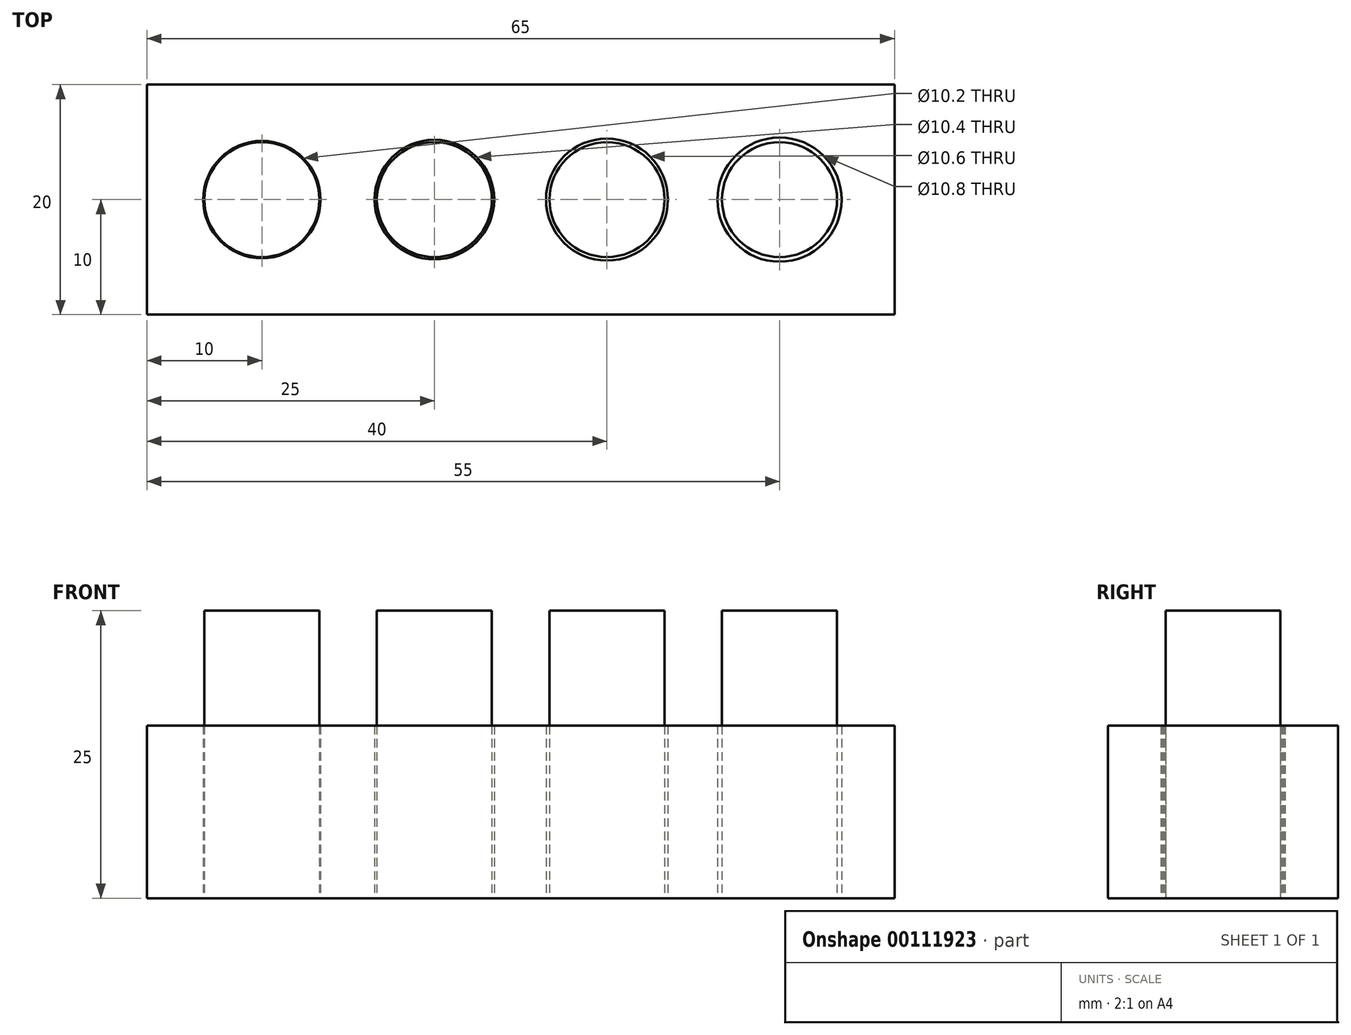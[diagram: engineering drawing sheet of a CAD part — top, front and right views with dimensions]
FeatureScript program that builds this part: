
annotation { "Feature Type Name" : "Feature", "Feature Type Description" : "" }
export const myFeature = defineFeature(function(context is Context, id is Id, definition is map)
    precondition{}
    {
        {
            var Q0;
            Q0=qCreatedBy(makeId("Top.planeOp"),FACE);
            var sketch = newSketch(context, id + "F0", { "sketchPlane" : qUnion([Q0])});
            skCircle(sketch, "E0", {"center": v(0, 0) * mm, "radius": 5 * mm});
            skCircle(sketch, "E1.1.0.0", {"center": v(15, 0) * mm, "radius": 5 * mm});
            skCircle(sketch, "E1.2.0.0", {"center": v(30, 0) * mm, "radius": 5 * mm});
            skCircle(sketch, "E1.3.0.0", {"center": v(45, 0) * mm, "radius": 5 * mm});
            skLineSegment(sketch, "E1.direction1", {"start": v(0, 0) * mm, "end": v(15, 0) * mm, "construction": true});
            skLineSegment(sketch, "E2.bottom", {"start": v(-10, 10) * mm, "end": v(55, 10) * mm});
            skLineSegment(sketch, "E2.top", {"start": v(-10, -10) * mm, "end": v(55, -10) * mm});
            skLineSegment(sketch, "E2.left", {"start": v(-10, 10) * mm, "end": v(-10, -10) * mm});
            skLineSegment(sketch, "E2.right", {"start": v(55, 10) * mm, "end": v(55, -10) * mm});
            skCircle(sketch, "E3.0", {"center": v(0, 0) * mm, "radius": 5.1 * mm});
            skCircle(sketch, "E4.0", {"center": v(15, 0) * mm, "radius": 5.2 * mm});
            skCircle(sketch, "E5.0", {"center": v(30, 0) * mm, "radius": 5.3 * mm});
            skCircle(sketch, "E6.0", {"center": v(45, 0) * mm, "radius": 5.4 * mm});
            skSolve(sketch);
        }
        {
            var Q0;
            Q0=makeQuery(id+"F0.imprint","IMPRINT",FACE,{"disambiguationData":[TD([[makeQuery(id+"F0.imprint","IMPRINT",EDGE,{"derivedFrom":sQuery(id+"F0.wireOp",EDGE,"E2.bottom")}),-1.0]])]});
            extrude(context, id + "F1", {"entities" : qUnion([Q0]), "depth" : 15 * mm});
        }
        {
            var Q0;
            Q0=makeQuery(id+"F0.imprint","IMPRINT",FACE,{"disambiguationData":[TD([[makeQuery(id+"F0.imprint","IMPRINT",EDGE,{"derivedFrom":sQuery(id+"F0.wireOp",EDGE,"E0")}),1.0]])]});
            var Q1;
            Q1=makeQuery(id+"F0.imprint","IMPRINT",FACE,{"disambiguationData":[TD([[makeQuery(id+"F0.imprint","IMPRINT",EDGE,{"derivedFrom":sQuery(id+"F0.wireOp",EDGE,"E1.1.0.0")}),1.0]])]});
            var Q2;
            Q2=makeQuery(id+"F0.imprint","IMPRINT",FACE,{"disambiguationData":[TD([[makeQuery(id+"F0.imprint","IMPRINT",EDGE,{"derivedFrom":sQuery(id+"F0.wireOp",EDGE,"E1.2.0.0")}),1.0]])]});
            var Q3;
            Q3=makeQuery(id+"F0.imprint","IMPRINT",FACE,{"disambiguationData":[TD([[makeQuery(id+"F0.imprint","IMPRINT",EDGE,{"derivedFrom":sQuery(id+"F0.wireOp",EDGE,"E1.3.0.0")}),1.0]])]});
            extrude(context, id + "F2", {"entities" : qUnion([Q0, Q1, Q2, Q3]), "depth" : 25 * mm});
        }
    });
